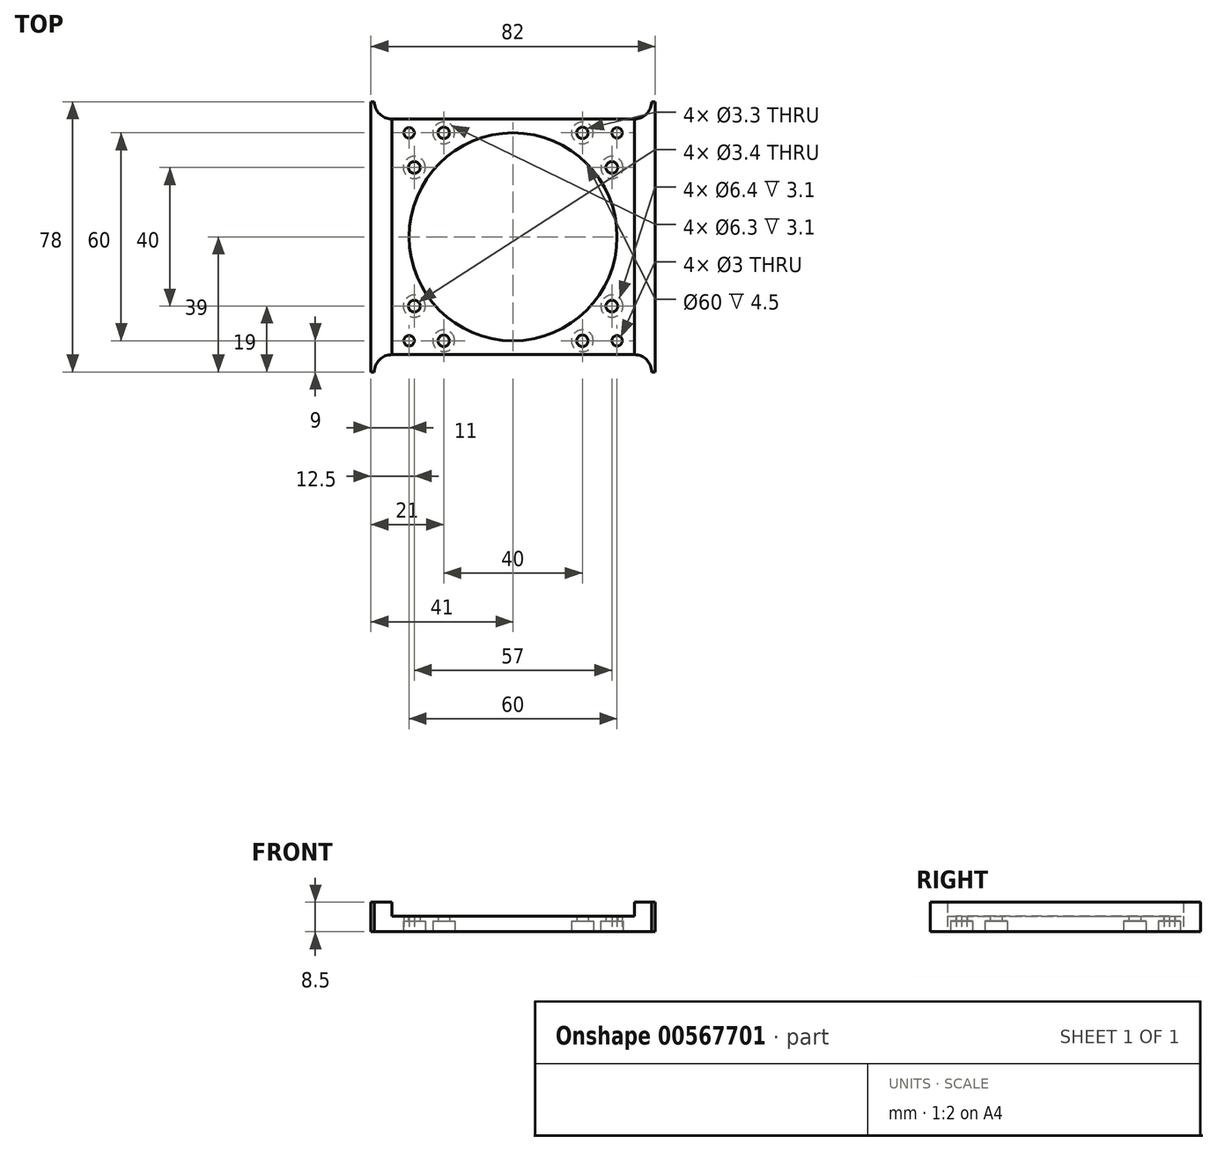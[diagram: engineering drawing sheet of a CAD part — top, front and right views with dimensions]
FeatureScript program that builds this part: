
annotation { "Feature Type Name" : "Feature", "Feature Type Description" : "" }
export const myFeature = defineFeature(function(context is Context, id is Id, definition is map)
    precondition{}
    {
        {
            var Q0;
            Q0=qCreatedBy(makeId("Top.planeOp"),FACE);
            var sketch = newSketch(context, id + "F0", { "sketchPlane" : qUnion([Q0])});
            skLineSegment(sketch, "E0.bottom", {"start": v(0, 0) * mm, "end": v(1, 0) * mm});
            skLineSegment(sketch, "E0.top", {"start": v(0, 78) * mm, "end": v(1, 78) * mm});
            skLineSegment(sketch, "E0.left", {"start": v(0, 0) * mm, "end": v(0, 78) * mm});
            skLineSegment(sketch, "E0.right", {"start": v(82, 0) * mm, "end": v(82, 78) * mm});
            skArc(sketch, "E1", {"start": v(6, 73) * mm, "mid": v(2.46, 74.46) * mm, "end": v(1, 78) * mm});
            skLineSegment(sketch, "E2", {"start": v(82, 78) * mm, "end": v(81, 78) * mm});
            skArc(sketch, "E3", {"start": v(76, 73) * mm, "mid": v(79.54, 74.46) * mm, "end": v(81, 78) * mm});
            skLineSegment(sketch, "E4", {"start": v(6, 73) * mm, "end": v(76, 73) * mm});
            skLineSegment(sketch, "E5.trimOffspring", {"start": v(81, 78) * mm, "end": v(82, 78) * mm});
            skLineSegment(sketch, "E6", {"start": v(6, 5) * mm, "end": v(76, 5) * mm});
            skArc(sketch, "E7", {"start": v(1, 0) * mm, "mid": v(2.46, 3.54) * mm, "end": v(6, 5) * mm});
            skArc(sketch, "E8", {"start": v(81, 0) * mm, "mid": v(79.54, 3.54) * mm, "end": v(76, 5) * mm});
            skLineSegment(sketch, "E9.trimOffspring", {"start": v(81, 0) * mm, "end": v(82, 0) * mm});
            skLineSegment(sketch, "E10", {"start": v(0, 39) * mm, "end": v(82, 39) * mm});
            skCircle(sketch, "E11", {"center": v(41, 39) * mm, "radius": 30 * mm});
            skSolve(sketch);
        }
        {
            var Q0;
            {var subQ5=sQuery(id+"F0.wireOp",EDGE,"E0.top");Q0=makeQuery(id+"F0.imprint","IMPRINT",FACE,{"disambiguationData":[TD([[makeQuery(id+"F0.imprint","IMPRINT",EDGE,{"derivedFrom":subQ5}),-1.0]])]});}
            var Q1;
            {var subQ0=sQuery(id+"F0.wireOp",EDGE,"E0.bottom");Q1=makeQuery(id+"F0.imprint","IMPRINT",FACE,{"disambiguationData":[TD([[makeQuery(id+"F0.imprint","IMPRINT",EDGE,{"derivedFrom":subQ0}),1.0]])]});}
            extrude(context, id + "F1", {"entities" : qUnion([Q0, Q1]), "depth" : 8.5 * mm, "offsetDistance" : 25 * mm});
        }
        {
            var Q0;
            Q0=makeQuery(id+"F1.opExtrude","CAP_FACE",FACE,{"disambiguationData":[OSD([sQuery(id+"F0.wireOp",EDGE,"E0.left"),sQuery(id+"F0.wireOp",EDGE,"E0.right"),sQuery(id+"F0.wireOp",EDGE,"E0.top"),sQuery(id+"F0.wireOp",EDGE,"E1"),sQuery(id+"F0.wireOp",EDGE,"E3"),sQuery(id+"F0.wireOp",EDGE,"E4"),sQuery(id+"F0.wireOp",EDGE,"E5.trimOffspring"),sQuery(id+"F0.wireOp",EDGE,"E0.bottom"),sQuery(id+"F0.wireOp",EDGE,"E6"),sQuery(id+"F0.wireOp",EDGE,"E7"),sQuery(id+"F0.wireOp",EDGE,"E8"),sQuery(id+"F0.wireOp",EDGE,"E9.trimOffspring"),sQuery(id+"F0.wireOp",EDGE,"E11")])],"isStart":false});
            var sketch = newSketch(context, id + "F2", { "sketchPlane" : qUnion([Q0])});
            skLineSegment(sketch, "E12.bottom", {"start": v(76, 5) * mm, "end": v(6, 5) * mm});
            skLineSegment(sketch, "E12.top", {"start": v(76, 73) * mm, "end": v(6, 73) * mm});
            skLineSegment(sketch, "E12.left", {"start": v(76, 5) * mm, "end": v(76, 73) * mm});
            skLineSegment(sketch, "E12.right", {"start": v(6, 5) * mm, "end": v(6, 73) * mm});
            skPoint(sketch, "E12.middle", {"position": v(41, 39) * mm});
            skSolve(sketch);
        }
        {
            var Q0;
            Q0=makeQuery(id+"F2.imprint","IMPRINT",FACE,{"disambiguationData":[TD([[makeQuery(id+"F2.imprint","IMPRINT",EDGE,{"derivedFrom":sQuery(id+"F2.wireOp",EDGE,"E12.bottom")}),1.0]])]});
            extrude(context, id + "F3", {"entities" : qUnion([Q0]), "operationType" : NewBodyOperationType.REMOVE, "oppositeDirection" : true, "depth" : 4 * mm, "offsetDistance" : 25 * mm});
        }
        {
            var Q0;
            Q0=makeQuery(id+"F1.opExtrude","CAP_FACE",FACE,{"disambiguationData":[OSD([sQuery(id+"F0.wireOp",EDGE,"E0.left"),sQuery(id+"F0.wireOp",EDGE,"E0.right"),sQuery(id+"F0.wireOp",EDGE,"E0.top"),sQuery(id+"F0.wireOp",EDGE,"E1"),sQuery(id+"F0.wireOp",EDGE,"E3"),sQuery(id+"F0.wireOp",EDGE,"E4"),sQuery(id+"F0.wireOp",EDGE,"E5.trimOffspring"),sQuery(id+"F0.wireOp",EDGE,"E0.bottom"),sQuery(id+"F0.wireOp",EDGE,"E6"),sQuery(id+"F0.wireOp",EDGE,"E7"),sQuery(id+"F0.wireOp",EDGE,"E8"),sQuery(id+"F0.wireOp",EDGE,"E9.trimOffspring"),sQuery(id+"F0.wireOp",EDGE,"E11")])],"isStart":true});
            var sketch = newSketch(context, id + "F4", { "sketchPlane" : qUnion([Q0])});
            skLineSegment(sketch, "E13", {"start": v(41, -39) * mm, "end": v(12.5, -39) * mm});
            skLineSegment(sketch, "E14", {"start": v(12.5, -39) * mm, "end": v(12.5, -19) * mm});
            skLineSegment(sketch, "E15", {"start": v(12.5, -39) * mm, "end": v(12.5, -59) * mm});
            skLineSegment(sketch, "E16", {"start": v(14.2, -19) * mm, "end": v(67.8, -19) * mm});
            skLineSegment(sketch, "E17", {"start": v(69.5, -19) * mm, "end": v(69.5, -59) * mm});
            skCircle(sketch, "E18", {"center": v(12.5, -19) * mm, "radius": 1.7 * mm});
            skCircle(sketch, "E19", {"center": v(12.5, -59) * mm, "radius": 1.7 * mm});
            skCircle(sketch, "E20", {"center": v(69.5, -19) * mm, "radius": 1.7 * mm});
            skCircle(sketch, "E21", {"center": v(69.5, -59) * mm, "radius": 1.7 * mm});
            skSolve(sketch);
        }
        {
            var Q0;
            {var subQ0=sQuery(id+"F4.wireOp",EDGE,"E18");var subQ1=makeQuery(id+"F4.imprint","INTERSECT",VERTEX,{"derivedFrom":[sQuery(id+"F4.wireOp",EDGE,"E16"),subQ0]});Q0=makeQuery(id+"F4.imprint","IMPRINT",FACE,{"disambiguationData":[TD([[makeQuery(id+"F4.imprint","IMPRINT",EDGE,{"disambiguationData":[TD([[subQ1,-1.0]])],"derivedFrom":subQ0}),1.0]])]});}
            var Q1;
            Q1=makeQuery(id+"F4.imprint","IMPRINT",FACE,{"disambiguationData":[TD([[makeQuery(id+"F4.imprint","IMPRINT",EDGE,{"derivedFrom":sQuery(id+"F4.wireOp",EDGE,"E19")}),1.0]])]});
            var Q2;
            Q2=makeQuery(id+"F4.imprint","IMPRINT",FACE,{"disambiguationData":[TD([[makeQuery(id+"F4.imprint","IMPRINT",EDGE,{"derivedFrom":sQuery(id+"F4.wireOp",EDGE,"E21")}),1.0]])]});
            var Q3;
            {var subQ0=sQuery(id+"F4.wireOp",EDGE,"E20");var subQ1=makeQuery(id+"F4.imprint","INTERSECT",VERTEX,{"derivedFrom":[sQuery(id+"F4.wireOp",EDGE,"E16"),subQ0]});Q3=makeQuery(id+"F4.imprint","IMPRINT",FACE,{"disambiguationData":[TD([[makeQuery(id+"F4.imprint","IMPRINT",EDGE,{"disambiguationData":[TD([[subQ1,-1.0]])],"derivedFrom":subQ0}),1.0]])]});}
            extrude(context, id + "F5", {"entities" : qUnion([Q0, Q1, Q2, Q3]), "operationType" : NewBodyOperationType.REMOVE, "oppositeDirection" : true, "depth" : 25 * mm, "offsetDistance" : 25 * mm});
        }
        {
            var Q0;
            Q0=makeQuery(id+"F1.opExtrude","CAP_FACE",FACE,{"disambiguationData":[OSD([sQuery(id+"F0.wireOp",EDGE,"E0.left"),sQuery(id+"F0.wireOp",EDGE,"E0.right"),sQuery(id+"F0.wireOp",EDGE,"E0.top"),sQuery(id+"F0.wireOp",EDGE,"E1"),sQuery(id+"F0.wireOp",EDGE,"E3"),sQuery(id+"F0.wireOp",EDGE,"E4"),sQuery(id+"F0.wireOp",EDGE,"E5.trimOffspring"),sQuery(id+"F0.wireOp",EDGE,"E0.bottom"),sQuery(id+"F0.wireOp",EDGE,"E6"),sQuery(id+"F0.wireOp",EDGE,"E7"),sQuery(id+"F0.wireOp",EDGE,"E8"),sQuery(id+"F0.wireOp",EDGE,"E9.trimOffspring"),sQuery(id+"F0.wireOp",EDGE,"E11")])],"isStart":true});
            var sketch = newSketch(context, id + "F6", { "sketchPlane" : qUnion([Q0])});
            skCircle(sketch, "E22", {"center": v(12.5, -19) * mm, "radius": 3.2 * mm});
            skCircle(sketch, "E23", {"center": v(69.5, -19) * mm, "radius": 3.2 * mm});
            skCircle(sketch, "E24", {"center": v(69.5, -59) * mm, "radius": 3.2 * mm});
            skCircle(sketch, "E25", {"center": v(12.5, -59) * mm, "radius": 3.2 * mm});
            skSolve(sketch);
        }
        {
            var Q0;
            Q0=makeQuery(id+"F6.imprint","IMPRINT",FACE,{"disambiguationData":[TD([[makeQuery(id+"F6.imprint","IMPRINT",EDGE,{"derivedFrom":sQuery(id+"F6.wireOp",EDGE,"E22")}),1.0]])]});
            var Q1;
            Q1=makeQuery(id+"F6.imprint","IMPRINT",FACE,{"disambiguationData":[TD([[makeQuery(id+"F6.imprint","IMPRINT",EDGE,{"derivedFrom":sQuery(id+"F6.wireOp",EDGE,"E25")}),1.0]])]});
            var Q2;
            Q2=makeQuery(id+"F6.imprint","IMPRINT",FACE,{"disambiguationData":[TD([[makeQuery(id+"F6.imprint","IMPRINT",EDGE,{"derivedFrom":sQuery(id+"F6.wireOp",EDGE,"E23")}),1.0]])]});
            var Q3;
            Q3=makeQuery(id+"F6.imprint","IMPRINT",FACE,{"disambiguationData":[TD([[makeQuery(id+"F6.imprint","IMPRINT",EDGE,{"derivedFrom":sQuery(id+"F6.wireOp",EDGE,"E24")}),1.0]])]});
            extrude(context, id + "F7", {"entities" : qUnion([Q0, Q1, Q2, Q3]), "operationType" : NewBodyOperationType.REMOVE, "oppositeDirection" : true, "depth" : 3.1 * mm, "offsetDistance" : 25 * mm});
        }
        {
            var Q0;
            Q0=makeQuery(id+"F1.opExtrude","CAP_FACE",FACE,{"disambiguationData":[OSD([sQuery(id+"F0.wireOp",EDGE,"E0.left"),sQuery(id+"F0.wireOp",EDGE,"E0.right"),sQuery(id+"F0.wireOp",EDGE,"E0.top"),sQuery(id+"F0.wireOp",EDGE,"E1"),sQuery(id+"F0.wireOp",EDGE,"E3"),sQuery(id+"F0.wireOp",EDGE,"E4"),sQuery(id+"F0.wireOp",EDGE,"E5.trimOffspring"),sQuery(id+"F0.wireOp",EDGE,"E0.bottom"),sQuery(id+"F0.wireOp",EDGE,"E6"),sQuery(id+"F0.wireOp",EDGE,"E7"),sQuery(id+"F0.wireOp",EDGE,"E8"),sQuery(id+"F0.wireOp",EDGE,"E9.trimOffspring"),sQuery(id+"F0.wireOp",EDGE,"E11")])],"isStart":true});
            var sketch = newSketch(context, id + "F8", { "sketchPlane" : qUnion([Q0])});
            skLineSegment(sketch, "E26", {"start": v(41, -39) * mm, "end": v(41, -9) * mm});
            skPoint(sketch, "E26.endSnap0", {"position": v(41, -5) * mm});
            skLineSegment(sketch, "E27", {"start": v(41, -9) * mm, "end": v(61, -9) * mm});
            skLineSegment(sketch, "E28", {"start": v(61, -9) * mm, "end": v(61, -69) * mm});
            skLineSegment(sketch, "E29", {"start": v(61, -69) * mm, "end": v(21, -69) * mm});
            skLineSegment(sketch, "E30", {"start": v(41, -9) * mm, "end": v(21, -9) * mm});
            skCircle(sketch, "E31", {"center": v(21, -9) * mm, "radius": 1.65 * mm});
            skCircle(sketch, "E32", {"center": v(61, -9) * mm, "radius": 1.65 * mm});
            skCircle(sketch, "E33", {"center": v(21, -69) * mm, "radius": 1.65 * mm});
            skCircle(sketch, "E34", {"center": v(61, -69) * mm, "radius": 1.65 * mm});
            skSolve(sketch);
        }
        {
            var Q0;
            Q0 = qSketchRegion(id + "F8", true);
            extrude(context, id + "F9", {"entities" : qUnion([Q0]), "operationType" : NewBodyOperationType.REMOVE, "oppositeDirection" : true, "depth" : 25 * mm, "offsetDistance" : 25 * mm});
        }
        {
            var Q0;
            Q0=makeQuery(id+"F1.opExtrude","CAP_FACE",FACE,{"disambiguationData":[OSD([sQuery(id+"F0.wireOp",EDGE,"E0.left"),sQuery(id+"F0.wireOp",EDGE,"E0.right"),sQuery(id+"F0.wireOp",EDGE,"E0.top"),sQuery(id+"F0.wireOp",EDGE,"E1"),sQuery(id+"F0.wireOp",EDGE,"E3"),sQuery(id+"F0.wireOp",EDGE,"E4"),sQuery(id+"F0.wireOp",EDGE,"E5.trimOffspring"),sQuery(id+"F0.wireOp",EDGE,"E0.bottom"),sQuery(id+"F0.wireOp",EDGE,"E6"),sQuery(id+"F0.wireOp",EDGE,"E7"),sQuery(id+"F0.wireOp",EDGE,"E8"),sQuery(id+"F0.wireOp",EDGE,"E9.trimOffspring"),sQuery(id+"F0.wireOp",EDGE,"E11")])],"isStart":true});
            var sketch = newSketch(context, id + "F10", { "sketchPlane" : qUnion([Q0])});
            skCircle(sketch, "E35", {"center": v(21, -9) * mm, "radius": 3.15 * mm});
            skCircle(sketch, "E36", {"center": v(61, -9) * mm, "radius": 3.15 * mm});
            skCircle(sketch, "E37", {"center": v(61, -69) * mm, "radius": 3.15 * mm});
            skCircle(sketch, "E38", {"center": v(21, -69) * mm, "radius": 3.15 * mm});
            skSolve(sketch);
        }
        {
            var Q0;
            Q0 = qSketchRegion(id + "F10", true);
            extrude(context, id + "F11", {"entities" : qUnion([Q0]), "operationType" : NewBodyOperationType.REMOVE, "oppositeDirection" : true, "depth" : 3.1 * mm, "offsetDistance" : 25 * mm});
        }
        {
            var Q0;
            Q0=makeQuery(id+"F1.opExtrude","CAP_FACE",FACE,{"disambiguationData":[OSD([sQuery(id+"F0.wireOp",EDGE,"E0.left"),sQuery(id+"F0.wireOp",EDGE,"E0.right"),sQuery(id+"F0.wireOp",EDGE,"E0.top"),sQuery(id+"F0.wireOp",EDGE,"E1"),sQuery(id+"F0.wireOp",EDGE,"E3"),sQuery(id+"F0.wireOp",EDGE,"E4"),sQuery(id+"F0.wireOp",EDGE,"E5.trimOffspring"),sQuery(id+"F0.wireOp",EDGE,"E0.bottom"),sQuery(id+"F0.wireOp",EDGE,"E6"),sQuery(id+"F0.wireOp",EDGE,"E7"),sQuery(id+"F0.wireOp",EDGE,"E8"),sQuery(id+"F0.wireOp",EDGE,"E9.trimOffspring"),sQuery(id+"F0.wireOp",EDGE,"E11")])],"isStart":true});
            var sketch = newSketch(context, id + "F12", { "sketchPlane" : qUnion([Q0])});
            skLineSegment(sketch, "E39.bottom", {"start": v(71, -69) * mm, "end": v(11, -69) * mm});
            skLineSegment(sketch, "E39.top", {"start": v(71, -9) * mm, "end": v(11, -9) * mm});
            skLineSegment(sketch, "E39.left", {"start": v(71, -69) * mm, "end": v(71, -9) * mm});
            skLineSegment(sketch, "E39.right", {"start": v(11, -69) * mm, "end": v(11, -9) * mm});
            skPoint(sketch, "E39.middle", {"position": v(41, -39) * mm});
            skCircle(sketch, "E40", {"center": v(11, -9) * mm, "radius": 1.5 * mm});
            skCircle(sketch, "E41", {"center": v(11, -69) * mm, "radius": 1.5 * mm});
            skCircle(sketch, "E42", {"center": v(71, -69) * mm, "radius": 1.5 * mm});
            skCircle(sketch, "E43", {"center": v(71, -9) * mm, "radius": 1.5 * mm});
            skSolve(sketch);
        }
        {
            var Q0;
            {var subQ0=sQuery(id+"F12.wireOp",EDGE,"E39.right");var subQ1=sQuery(id+"F12.wireOp",EDGE,"E39.top");var subQ2=makeQuery(id+"F12.imprint","INTERSECT",VERTEX,{"derivedFrom":[subQ1,subQ0]});Q0=makeQuery(id+"F12.imprint","IMPRINT",FACE,{"disambiguationData":[TD([[makeQuery(id+"F12.imprint","IMPRINT",EDGE,{"disambiguationData":[TD([[subQ2,1.0]])],"derivedFrom":subQ1}),-1.0]])]});}
            var Q1;
            {var subQ0=sQuery(id+"F12.wireOp",EDGE,"E39.right");var subQ1=sQuery(id+"F12.wireOp",EDGE,"E39.top");var subQ2=makeQuery(id+"F12.imprint","INTERSECT",VERTEX,{"derivedFrom":[subQ1,subQ0]});Q1=makeQuery(id+"F12.imprint","IMPRINT",FACE,{"disambiguationData":[TD([[makeQuery(id+"F12.imprint","IMPRINT",EDGE,{"disambiguationData":[TD([[subQ2,1.0]])],"derivedFrom":subQ1}),1.0]])]});}
            var Q2;
            {var subQ0=sQuery(id+"F12.wireOp",EDGE,"E39.left");var subQ1=sQuery(id+"F12.wireOp",EDGE,"E39.top");var subQ2=makeQuery(id+"F12.imprint","INTERSECT",VERTEX,{"derivedFrom":[subQ1,subQ0]});Q2=makeQuery(id+"F12.imprint","IMPRINT",FACE,{"disambiguationData":[TD([[makeQuery(id+"F12.imprint","IMPRINT",EDGE,{"disambiguationData":[TD([[subQ2,-1.0]])],"derivedFrom":subQ1}),1.0]])]});}
            var Q3;
            {var subQ0=sQuery(id+"F12.wireOp",EDGE,"E39.left");var subQ1=sQuery(id+"F12.wireOp",EDGE,"E39.top");var subQ2=makeQuery(id+"F12.imprint","INTERSECT",VERTEX,{"derivedFrom":[subQ1,subQ0]});Q3=makeQuery(id+"F12.imprint","IMPRINT",FACE,{"disambiguationData":[TD([[makeQuery(id+"F12.imprint","IMPRINT",EDGE,{"disambiguationData":[TD([[subQ2,-1.0]])],"derivedFrom":subQ1}),-1.0]])]});}
            var Q4;
            {var subQ0=sQuery(id+"F12.wireOp",EDGE,"E39.left");var subQ1=sQuery(id+"F12.wireOp",EDGE,"E39.bottom");var subQ2=makeQuery(id+"F12.imprint","INTERSECT",VERTEX,{"derivedFrom":[subQ1,subQ0]});Q4=makeQuery(id+"F12.imprint","IMPRINT",FACE,{"disambiguationData":[TD([[makeQuery(id+"F12.imprint","IMPRINT",EDGE,{"disambiguationData":[TD([[subQ2,-1.0]])],"derivedFrom":subQ1}),-1.0]])]});}
            var Q5;
            {var subQ0=sQuery(id+"F12.wireOp",EDGE,"E39.left");var subQ1=sQuery(id+"F12.wireOp",EDGE,"E39.bottom");var subQ2=makeQuery(id+"F12.imprint","INTERSECT",VERTEX,{"derivedFrom":[subQ1,subQ0]});Q5=makeQuery(id+"F12.imprint","IMPRINT",FACE,{"disambiguationData":[TD([[makeQuery(id+"F12.imprint","IMPRINT",EDGE,{"disambiguationData":[TD([[subQ2,-1.0]])],"derivedFrom":subQ1}),1.0]])]});}
            var Q6;
            {var subQ0=sQuery(id+"F12.wireOp",EDGE,"E39.right");var subQ1=sQuery(id+"F12.wireOp",EDGE,"E39.bottom");var subQ2=makeQuery(id+"F12.imprint","INTERSECT",VERTEX,{"derivedFrom":[subQ1,subQ0]});Q6=makeQuery(id+"F12.imprint","IMPRINT",FACE,{"disambiguationData":[TD([[makeQuery(id+"F12.imprint","IMPRINT",EDGE,{"disambiguationData":[TD([[subQ2,1.0]])],"derivedFrom":subQ1}),1.0]])]});}
            var Q7;
            {var subQ0=sQuery(id+"F12.wireOp",EDGE,"E39.right");var subQ1=sQuery(id+"F12.wireOp",EDGE,"E39.bottom");var subQ2=makeQuery(id+"F12.imprint","INTERSECT",VERTEX,{"derivedFrom":[subQ1,subQ0]});Q7=makeQuery(id+"F12.imprint","IMPRINT",FACE,{"disambiguationData":[TD([[makeQuery(id+"F12.imprint","IMPRINT",EDGE,{"disambiguationData":[TD([[subQ2,1.0]])],"derivedFrom":subQ1}),-1.0]])]});}
            extrude(context, id + "F13", {"entities" : qUnion([Q0, Q1, Q2, Q3, Q4, Q5, Q6, Q7]), "operationType" : NewBodyOperationType.REMOVE, "oppositeDirection" : true, "depth" : 25 * mm, "offsetDistance" : 25 * mm});
        }
    });
